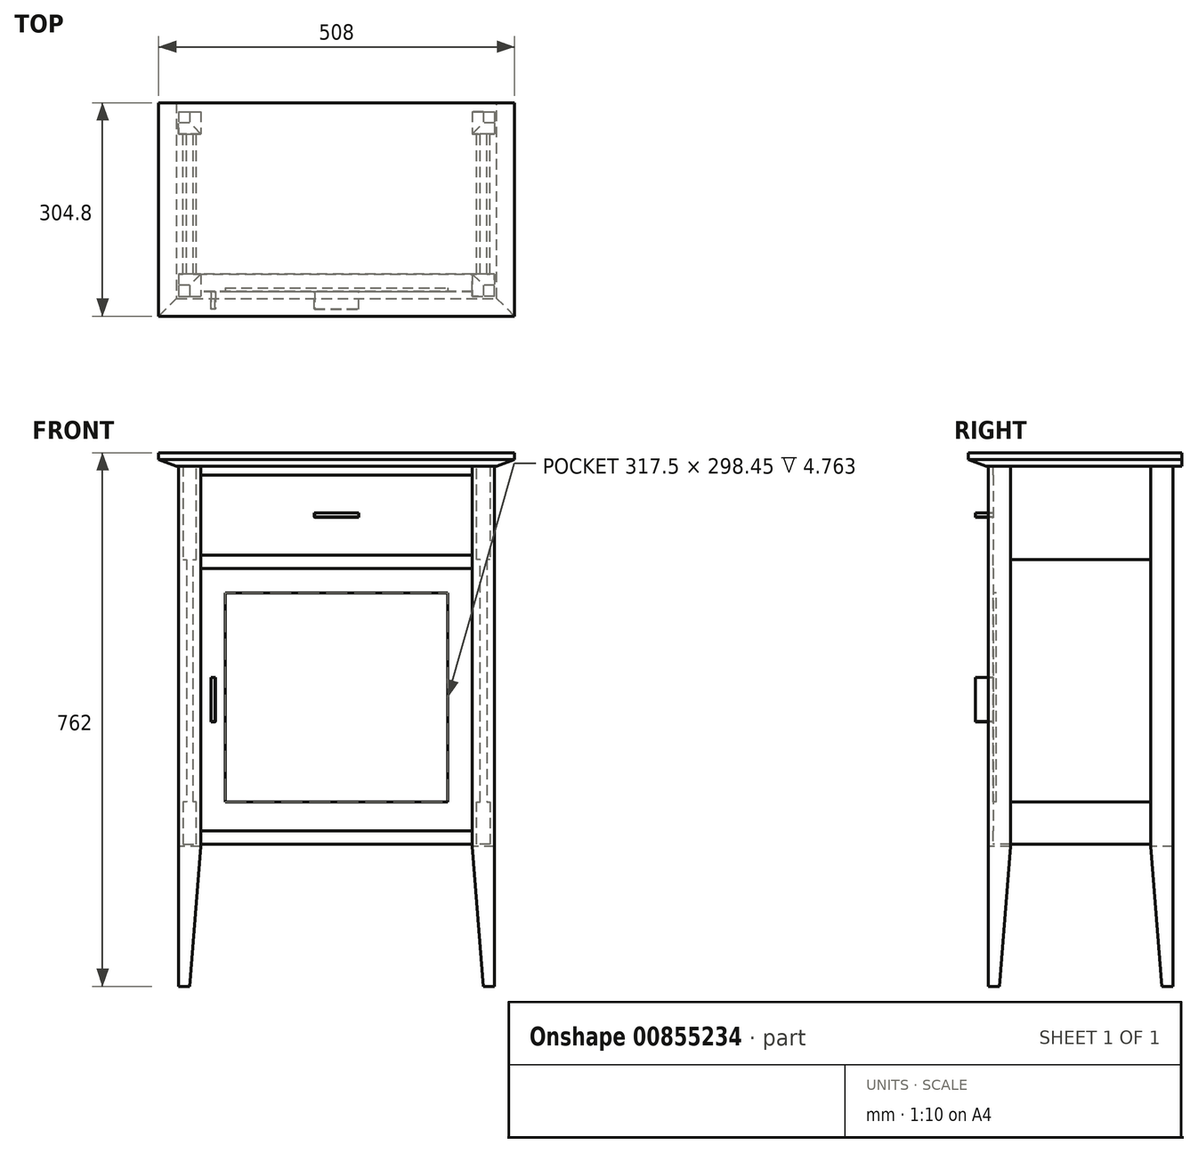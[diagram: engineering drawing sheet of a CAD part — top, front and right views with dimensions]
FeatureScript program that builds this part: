
annotation { "Feature Type Name" : "Feature", "Feature Type Description" : "" }
export const myFeature = defineFeature(function(context is Context, id is Id, definition is map)
    precondition{}
    {
        {
            var Q0;
            Q0=qCreatedBy(makeId("Top.planeOp"),FACE);
            var sketch = newSketch(context, id + "F0", { "sketchPlane" : qUnion([Q0])});
            skLineSegment(sketch, "E0", {"start": v(-209.55, 115.89) * mm, "end": v(209.55, 115.89) * mm, "construction": true});
            skLineSegment(sketch, "E1", {"start": v(209.55, 115.89) * mm, "end": v(209.55, -115.89) * mm, "construction": true});
            skLineSegment(sketch, "E2", {"start": v(209.55, -115.89) * mm, "end": v(-209.55, -115.89) * mm, "construction": true});
            skLineSegment(sketch, "E3", {"start": v(-209.55, -115.89) * mm, "end": v(-209.55, 115.89) * mm, "construction": true});
            skLineSegment(sketch, "E4", {"start": v(0, 115.89) * mm, "end": v(0, -115.89) * mm, "construction": true});
            skLineSegment(sketch, "E5", {"start": v(-209.55, 0) * mm, "end": v(209.55, 0) * mm, "construction": true});
            skPoint(sketch, "E6", {"position": v(0, 0) * mm});
            skLineSegment(sketch, "E7.bottom", {"start": v(-225.43, 131.76) * mm, "end": v(-193.68, 131.76) * mm});
            skLineSegment(sketch, "E7.top", {"start": v(-225.43, 100.01) * mm, "end": v(-193.68, 100.01) * mm});
            skLineSegment(sketch, "E7.left", {"start": v(-225.43, 131.76) * mm, "end": v(-225.43, 100.01) * mm});
            skLineSegment(sketch, "E7.right", {"start": v(-193.68, 131.76) * mm, "end": v(-193.68, 100.01) * mm});
            skPoint(sketch, "E7.middle", {"position": v(-209.55, 115.89) * mm});
            skLineSegment(sketch, "E8.bottom", {"start": v(193.67, 131.76) * mm, "end": v(225.42, 131.76) * mm});
            skLineSegment(sketch, "E8.top", {"start": v(193.67, 100.01) * mm, "end": v(225.42, 100.01) * mm});
            skLineSegment(sketch, "E8.left", {"start": v(193.67, 131.76) * mm, "end": v(193.67, 100.01) * mm});
            skLineSegment(sketch, "E8.right", {"start": v(225.42, 131.76) * mm, "end": v(225.42, 100.01) * mm});
            skPoint(sketch, "E8.middle", {"position": v(209.55, 115.89) * mm});
            skLineSegment(sketch, "E9.bottom", {"start": v(-225.42, -100.01) * mm, "end": v(-193.67, -100.01) * mm});
            skLineSegment(sketch, "E9.top", {"start": v(-225.42, -131.76) * mm, "end": v(-193.67, -131.76) * mm});
            skLineSegment(sketch, "E9.left", {"start": v(-225.42, -100.01) * mm, "end": v(-225.42, -131.76) * mm});
            skLineSegment(sketch, "E9.right", {"start": v(-193.67, -100.01) * mm, "end": v(-193.67, -131.76) * mm});
            skPoint(sketch, "E9.middle", {"position": v(-209.55, -115.89) * mm});
            skLineSegment(sketch, "E10.bottom", {"start": v(225.43, -131.76) * mm, "end": v(193.68, -131.76) * mm});
            skLineSegment(sketch, "E10.top", {"start": v(225.43, -100.01) * mm, "end": v(193.68, -100.01) * mm});
            skLineSegment(sketch, "E10.left", {"start": v(225.43, -131.76) * mm, "end": v(225.43, -100.01) * mm});
            skLineSegment(sketch, "E10.right", {"start": v(193.68, -131.76) * mm, "end": v(193.68, -100.01) * mm});
            skPoint(sketch, "E10.middle", {"position": v(209.55, -115.89) * mm});
            skSolve(sketch);
        }
        {
            var Q0;
            Q0 = qSketchRegion(id + "F0", true);
            extrude(context, id + "F1", {"entities" : qUnion([Q0]), "depth" : 742.95 * mm, "offsetDistance" : 25.4 * mm});
        }
        {
            var Q0;
            Q0=makeQuery(id+"F1.opExtrude","SWEPT_FACE",FACE,{"disambiguationData":[OSD([sQuery(id+"F0.wireOp",EDGE,"E7.top")])]});
            var sketch = newSketch(context, id + "F2", { "sketchPlane" : qUnion([Q0])});
            skLineSegment(sketch, "E11", {"start": v(-209.55, 742.95) * mm, "end": v(-209.55, 0) * mm, "construction": true});
            skLineSegment(sketch, "E12", {"start": v(-219.08, 742.95) * mm, "end": v(-219.08, 609.6) * mm});
            skLineSegment(sketch, "E13", {"start": v(-219.08, 609.6) * mm, "end": v(-200.03, 609.6) * mm});
            skLineSegment(sketch, "E14", {"start": v(-200.03, 609.6) * mm, "end": v(-200.03, 742.95) * mm});
            skLineSegment(sketch, "E15", {"start": v(-200.03, 742.95) * mm, "end": v(-219.08, 742.95) * mm});
            skLineSegment(sketch, "E16", {"start": v(-214.31, 609.6) * mm, "end": v(-214.31, 263.53) * mm});
            skLineSegment(sketch, "E17", {"start": v(-214.31, 263.53) * mm, "end": v(-204.79, 263.53) * mm});
            skLineSegment(sketch, "E18", {"start": v(-204.79, 263.53) * mm, "end": v(-204.79, 609.6) * mm});
            skLineSegment(sketch, "E19", {"start": v(-219.08, 263.53) * mm, "end": v(-219.08, 203.2) * mm});
            skLineSegment(sketch, "E20", {"start": v(-219.08, 203.2) * mm, "end": v(-200.03, 203.2) * mm});
            skLineSegment(sketch, "E21", {"start": v(-200.03, 203.2) * mm, "end": v(-200.03, 263.53) * mm});
            skLineSegment(sketch, "E22", {"start": v(-200.03, 263.53) * mm, "end": v(-219.08, 263.53) * mm});
            skLineSegment(sketch, "E23", {"start": v(-193.68, 0) * mm, "end": v(-193.68, 200.03) * mm});
            skLineSegment(sketch, "E24", {"start": v(-193.68, 200.03) * mm, "end": v(-209.55, 0) * mm});
            skLineSegment(sketch, "E25", {"start": v(-209.55, 0) * mm, "end": v(-193.68, 0) * mm});
            skLineSegment(sketch, "E26", {"start": v(0, 0) * mm, "end": v(0, 787.82) * mm, "construction": true});
            skLineSegment(sketch, "E27.MirrorCS", {"start": v(200.03, 742.95) * mm, "end": v(219.08, 742.95) * mm});
            skLineSegment(sketch, "E28.MirrorCS", {"start": v(219.08, 742.95) * mm, "end": v(219.08, 609.6) * mm});
            skLineSegment(sketch, "E29.MirrorCS", {"start": v(200.03, 609.6) * mm, "end": v(200.03, 742.95) * mm});
            skLineSegment(sketch, "E30.MirrorCS", {"start": v(219.08, 609.6) * mm, "end": v(200.03, 609.6) * mm});
            skLineSegment(sketch, "E31.MirrorCS", {"start": v(214.31, 609.6) * mm, "end": v(214.31, 263.53) * mm});
            skLineSegment(sketch, "E32.MirrorCS", {"start": v(204.79, 263.53) * mm, "end": v(204.79, 609.6) * mm});
            skLineSegment(sketch, "E33.MirrorCS", {"start": v(200.03, 263.53) * mm, "end": v(219.08, 263.53) * mm});
            skLineSegment(sketch, "E34.MirrorCS", {"start": v(219.08, 263.53) * mm, "end": v(219.08, 203.2) * mm});
            skLineSegment(sketch, "E35.MirrorCS", {"start": v(200.03, 203.2) * mm, "end": v(200.03, 263.53) * mm});
            skLineSegment(sketch, "E36.MirrorCS", {"start": v(219.08, 203.2) * mm, "end": v(200.03, 203.2) * mm});
            skLineSegment(sketch, "E37.MirrorCS", {"start": v(193.68, 200.03) * mm, "end": v(209.55, 0) * mm});
            skLineSegment(sketch, "E38.MirrorCS", {"start": v(193.68, 0) * mm, "end": v(193.68, 200.03) * mm});
            skLineSegment(sketch, "E39.MirrorCS", {"start": v(209.55, 0) * mm, "end": v(193.68, 0) * mm});
            skSolve(sketch);
        }
        {
            var Q0;
            {var subQ3=sQuery(id+"F2.wireOp",EDGE,"E19");Q0=makeQuery(id+"F2.imprint","IMPRINT",FACE,{"disambiguationData":[TD([[makeQuery(id+"F2.imprint","IMPRINT",EDGE,{"derivedFrom":subQ3}),1.0]])]});}
            var Q1;
            {var subQ0=sQuery(id+"F2.wireOp",EDGE,"E16");Q1=makeQuery(id+"F2.imprint","IMPRINT",FACE,{"disambiguationData":[TD([[makeQuery(id+"F2.imprint","IMPRINT",EDGE,{"derivedFrom":subQ0}),1.0]])]});}
            var Q2;
            {var subQ4=sQuery(id+"F2.wireOp",EDGE,"E12");Q2=makeQuery(id+"F2.imprint","IMPRINT",FACE,{"disambiguationData":[TD([[makeQuery(id+"F2.imprint","IMPRINT",EDGE,{"derivedFrom":subQ4}),1.0]])]});}
            var Q3;
            Q3=makeQuery(id+"F2.imprint","IMPRINT",FACE,{"disambiguationData":[TD([[makeQuery(id+"F2.imprint","IMPRINT",EDGE,{"derivedFrom":sQuery(id+"F2.wireOp",EDGE,"E27.MirrorCS")}),-1.0]])]});
            var Q4;
            {var subQ0=sQuery(id+"F2.wireOp",EDGE,"E31.MirrorCS");Q4=makeQuery(id+"F2.imprint","IMPRINT",FACE,{"disambiguationData":[TD([[makeQuery(id+"F2.imprint","IMPRINT",EDGE,{"derivedFrom":subQ0}),-1.0]])]});}
            var Q5;
            {var subQ0=sQuery(id+"F2.wireOp",EDGE,"E34.MirrorCS");Q5=makeQuery(id+"F2.imprint","IMPRINT",FACE,{"disambiguationData":[TD([[makeQuery(id+"F2.imprint","IMPRINT",EDGE,{"derivedFrom":subQ0}),-1.0]])]});}
            extrude(context, id + "F3", {"entities" : qUnion([Q0, Q1, Q2, Q3, Q4, Q5]), "operationType" : NewBodyOperationType.ADD, "endBound" : BoundingType.UP_TO_NEXT, "depth" : 25.4 * mm, "offsetDistance" : 25.4 * mm});
        }
        {
            var Q0;
            Q0=makeQuery(id+"F2.imprint","IMPRINT",FACE,{"disambiguationData":[TD([[makeQuery(id+"F2.imprint","IMPRINT",EDGE,{"derivedFrom":sQuery(id+"F2.wireOp",EDGE,"E23")}),-1.0]])]});
            var Q1;
            Q1=makeQuery(id+"F2.imprint","IMPRINT",FACE,{"disambiguationData":[TD([[makeQuery(id+"F2.imprint","IMPRINT",EDGE,{"derivedFrom":sQuery(id+"F2.wireOp",EDGE,"E37.MirrorCS")}),-1.0]])]});
            extrude(context, id + "F4", {"entities" : qUnion([Q0, Q1]), "operationType" : NewBodyOperationType.REMOVE, "endBound" : BoundingType.THROUGH_ALL, "oppositeDirection" : true, "depth" : 25.4 * mm, "offsetDistance" : 25.4 * mm, "hasSecondDirection" : true, "secondDirectionBound" : SecondDirectionBoundingType.THROUGH_ALL, "secondDirectionOppositeDirection" : false, "secondDirectionDepth" : 25.4 * mm});
        }
        {
            var Q0;
            Q0=makeQuery(id+"F1.opExtrude","SWEPT_FACE",FACE,{"disambiguationData":[OSD([sQuery(id+"F0.wireOp",EDGE,"E9.left")])]});
            var sketch = newSketch(context, id + "F5", { "sketchPlane" : qUnion([Q0])});
            skLineSegment(sketch, "E40", {"start": v(100.01, 200.03) * mm, "end": v(115.89, 0) * mm});
            skLineSegment(sketch, "E41", {"start": v(115.89, 0) * mm, "end": v(100.01, 0) * mm});
            skLineSegment(sketch, "E42", {"start": v(100.01, 0) * mm, "end": v(100.01, 200.03) * mm});
            skLineSegment(sketch, "E43", {"start": v(0, 0) * mm, "end": v(0, 281.06) * mm, "construction": true});
            skLineSegment(sketch, "E44.MirrorCS", {"start": v(-100.01, 200.03) * mm, "end": v(-115.89, 0) * mm});
            skLineSegment(sketch, "E45.MirrorCS", {"start": v(-100.01, 0) * mm, "end": v(-100.01, 200.03) * mm});
            skLineSegment(sketch, "E46.MirrorCS", {"start": v(-115.89, 0) * mm, "end": v(-100.01, 0) * mm});
            skSolve(sketch);
        }
        {
            var Q0;
            Q0 = qSketchRegion(id + "F5", true);
            extrude(context, id + "F6", {"entities" : qUnion([Q0]), "operationType" : NewBodyOperationType.REMOVE, "endBound" : BoundingType.THROUGH_ALL, "oppositeDirection" : true, "depth" : 25.4 * mm, "offsetDistance" : 25.4 * mm});
        }
        {
            var Q0;
            Q0=makeQuery(id+"F1.opExtrude","SWEPT_FACE",FACE,{"disambiguationData":[OSD([sQuery(id+"F0.wireOp",EDGE,"E9.right")])]});
            var sketch = newSketch(context, id + "F7", { "sketchPlane" : qUnion([Q0])});
            skLineSegment(sketch, "E47.bottom", {"start": v(-100.01, 742.95) * mm, "end": v(-125.41, 742.95) * mm});
            skLineSegment(sketch, "E47.top", {"start": v(-100.01, 730.25) * mm, "end": v(-125.41, 730.25) * mm});
            skLineSegment(sketch, "E47.left", {"start": v(-100.01, 742.95) * mm, "end": v(-100.01, 730.25) * mm});
            skLineSegment(sketch, "E47.right", {"start": v(-125.41, 742.95) * mm, "end": v(-125.41, 730.25) * mm});
            skLineSegment(sketch, "E48.bottom", {"start": v(-100.01, 615.95) * mm, "end": v(-125.41, 615.95) * mm});
            skLineSegment(sketch, "E48.top", {"start": v(-100.01, 596.9) * mm, "end": v(-125.41, 596.9) * mm});
            skLineSegment(sketch, "E48.left", {"start": v(-100.01, 615.95) * mm, "end": v(-100.01, 596.9) * mm});
            skLineSegment(sketch, "E48.right", {"start": v(-125.41, 615.95) * mm, "end": v(-125.41, 596.9) * mm});
            skLineSegment(sketch, "E49", {"start": v(-125.02, 730.25) * mm, "end": v(-125.02, 615.95) * mm});
            skLineSegment(sketch, "E50", {"start": v(-100.01, 615.95) * mm, "end": v(-100.01, 730.25) * mm});
            skLineSegment(sketch, "E51.bottom", {"start": v(-100.01, 222.25) * mm, "end": v(-125.41, 222.25) * mm});
            skLineSegment(sketch, "E51.top", {"start": v(-100.01, 203.2) * mm, "end": v(-125.41, 203.2) * mm});
            skLineSegment(sketch, "E51.left", {"start": v(-100.01, 222.25) * mm, "end": v(-100.01, 203.2) * mm});
            skLineSegment(sketch, "E51.right", {"start": v(-125.41, 222.25) * mm, "end": v(-125.41, 203.2) * mm});
            skLineSegment(sketch, "E52", {"start": v(-125.02, 596.9) * mm, "end": v(-125.02, 222.25) * mm});
            skLineSegment(sketch, "E53", {"start": v(-100.01, 222.25) * mm, "end": v(-100.01, 596.9) * mm});
            skSolve(sketch);
        }
        {
            var Q0;
            Q0 = qSketchRegion(id + "F7", true);
            extrude(context, id + "F8", {"entities" : qUnion([Q0]), "operationType" : NewBodyOperationType.ADD, "endBound" : BoundingType.UP_TO_NEXT, "depth" : 25.4 * mm, "offsetDistance" : 25.4 * mm});
        }
        {
            var Q0;
            Q0=makeQuery(id+"F8.opExtrude","SWEPT_FACE",FACE,{"disambiguationData":[OSD([sQuery(id+"F7.wireOp",EDGE,"E52")])]});
            var sketch = newSketch(context, id + "F9", { "sketchPlane" : qUnion([Q0])});
            skLineSegment(sketch, "E54.0", {"start": v(-158.75, 257.18) * mm, "end": v(158.75, 257.18) * mm});
            skLineSegment(sketch, "E54.1", {"start": v(-158.75, 561.98) * mm, "end": v(-158.75, 257.18) * mm});
            skLineSegment(sketch, "E54.2", {"start": v(158.75, 561.98) * mm, "end": v(-158.75, 561.98) * mm});
            skLineSegment(sketch, "E54.3", {"start": v(158.75, 257.18) * mm, "end": v(158.75, 561.98) * mm});
            skLineSegment(sketch, "E55", {"start": v(-158.75, 263.53) * mm, "end": v(158.75, 263.53) * mm});
            skSolve(sketch);
        }
        {
            var Q0;
            {var subQ0=sQuery(id+"F9.wireOp",EDGE,"E54.2");Q0=makeQuery(id+"F9.imprint","IMPRINT",FACE,{"disambiguationData":[TD([[makeQuery(id+"F9.imprint","IMPRINT",EDGE,{"derivedFrom":subQ0}),1.0]])]});}
            extrude(context, id + "F10", {"entities" : qUnion([Q0]), "operationType" : NewBodyOperationType.REMOVE, "oppositeDirection" : true, "depth" : 4.76 * mm, "offsetDistance" : 25.4 * mm});
        }
        {
            var Q0;
            Q0=makeQuery(id+"F8.boolean.opBoolean","MERGE",FACE,{"derivedFrom":[makeQuery(id+"F3.boolean.opBoolean","MERGE",FACE,{"derivedFrom":[makeQuery(id+"F1.opExtrude","CAP_FACE",FACE,{"disambiguationData":[OSD([sQuery(id+"F0.wireOp",EDGE,"E7.bottom"),sQuery(id+"F0.wireOp",EDGE,"E7.top"),sQuery(id+"F0.wireOp",EDGE,"E7.left"),sQuery(id+"F0.wireOp",EDGE,"E7.right")])],"isStart":false}),makeQuery(id+"F1.opExtrude","CAP_FACE",FACE,{"disambiguationData":[OSD([sQuery(id+"F0.wireOp",EDGE,"E9.bottom"),sQuery(id+"F0.wireOp",EDGE,"E9.top"),sQuery(id+"F0.wireOp",EDGE,"E9.left"),sQuery(id+"F0.wireOp",EDGE,"E9.right")])],"isStart":false}),makeQuery(id+"F3.opExtrude","SWEPT_FACE",FACE,{"disambiguationData":[OSD([sQuery(id+"F2.wireOp",EDGE,"E15")])]})]}),makeQuery(id+"F3.boolean.opBoolean","MERGE",FACE,{"derivedFrom":[makeQuery(id+"F1.opExtrude","CAP_FACE",FACE,{"disambiguationData":[OSD([sQuery(id+"F0.wireOp",EDGE,"E8.bottom"),sQuery(id+"F0.wireOp",EDGE,"E8.top"),sQuery(id+"F0.wireOp",EDGE,"E8.left"),sQuery(id+"F0.wireOp",EDGE,"E8.right")])],"isStart":false}),makeQuery(id+"F1.opExtrude","CAP_FACE",FACE,{"disambiguationData":[OSD([sQuery(id+"F0.wireOp",EDGE,"E10.bottom"),sQuery(id+"F0.wireOp",EDGE,"E10.top"),sQuery(id+"F0.wireOp",EDGE,"E10.left"),sQuery(id+"F0.wireOp",EDGE,"E10.right")])],"isStart":false}),makeQuery(id+"F3.opExtrude","SWEPT_FACE",FACE,{"disambiguationData":[OSD([sQuery(id+"F2.wireOp",EDGE,"E27.MirrorCS")])]})]}),makeQuery(id+"F8.opExtrude","SWEPT_FACE",FACE,{"disambiguationData":[OSD([sQuery(id+"F7.wireOp",EDGE,"E47.bottom")])]})]});
            var sketch = newSketch(context, id + "F11", { "sketchPlane" : qUnion([Q0])});
            skLineSegment(sketch, "E56", {"start": v(0, 137.26) * mm, "end": v(0, -185.37) * mm, "construction": true});
            skLineSegment(sketch, "E57", {"start": v(-177.63, 0) * mm, "end": v(186.24, 0) * mm, "construction": true});
            skLineSegment(sketch, "E58", {"start": v(-254, 144.46) * mm, "end": v(254, 144.46) * mm});
            skLineSegment(sketch, "E59", {"start": v(254, 144.46) * mm, "end": v(254, -160.34) * mm});
            skLineSegment(sketch, "E60", {"start": v(254, -160.34) * mm, "end": v(-254, -160.34) * mm});
            skLineSegment(sketch, "E61", {"start": v(-254, -160.34) * mm, "end": v(-254, 144.46) * mm});
            skSolve(sketch);
        }
        {
            var Q0;
            Q0 = qSketchRegion(id + "F11", true);
            extrude(context, id + "F12", {"entities" : qUnion([Q0]), "operationType" : NewBodyOperationType.ADD, "depth" : 19.05 * mm, "offsetDistance" : 25.4 * mm});
        }
        {
            var Q0;
            Q0=makeQuery(id+"F12.opExtrude","SWEPT_FACE",FACE,{"disambiguationData":[OSD([sQuery(id+"F11.wireOp",EDGE,"E58")])]});
            var sketch = newSketch(context, id + "F13", { "sketchPlane" : qUnion([Q0])});
            skLineSegment(sketch, "E62", {"start": v(228.6, 742.95) * mm, "end": v(254, 752.48) * mm});
            skLineSegment(sketch, "E63", {"start": v(254, 752.48) * mm, "end": v(254, 742.95) * mm});
            skLineSegment(sketch, "E64", {"start": v(254, 742.95) * mm, "end": v(228.6, 742.95) * mm});
            skSolve(sketch);
        }
        {
            var Q0;
            Q0=makeQuery(id+"F13.imprint","IMPRINT",FACE,{"disambiguationData":[TD([[makeQuery(id+"F13.imprint","IMPRINT",EDGE,{"derivedFrom":sQuery(id+"F13.wireOp",EDGE,"E62")}),-1.0]])]});
            var Q1;
            Q1=makeQuery(id+"F1NDxMYOyf2uWx9_1.boolean.opBoolean","MERGE",EDGE,{"derivedFrom":[makeQuery(id+"F12.opExtrude","CAP_EDGE",EDGE,{"disambiguationData":[OSD([sQuery(id+"F11.wireOp",EDGE,"E61")])],"isStart":true}),makeQuery(id+"F1NDxMYOyf2uWx9_1.opExtrude","SWEPT_EDGE",EDGE,{"disambiguationData":[OSD([sQuery(id+"F13.wireOp",EDGE,"E63"),sQuery(id+"F13.wireOp",EDGE,"E64")])]})]});
            var Q2;
            Q2=makeQuery(id+"F12.opExtrude","CAP_EDGE",EDGE,{"disambiguationData":[OSD([sQuery(id+"F11.wireOp",EDGE,"E60")])],"isStart":true});
            var Q3;
            Q3=makeQuery(id+"F12.opExtrude","CAP_EDGE",EDGE,{"disambiguationData":[OSD([sQuery(id+"F11.wireOp",EDGE,"E59")])],"isStart":true});
            sweep(context, id + "F14", {"operationType" : NewBodyOperationType.REMOVE, "profiles" : qUnion([Q0]), "path" : qUnion([Q1, Q2, Q3])});
        }
        {
            var Q0;
            Q0=makeQuery(id+"F8.opExtrude","SWEPT_FACE",FACE,{"disambiguationData":[OSD([sQuery(id+"F7.wireOp",EDGE,"E49")])]});
            var sketch = newSketch(context, id + "F15", { "sketchPlane" : qUnion([Q0])});
            skLineSegment(sketch, "E65", {"start": v(0, 730.25) * mm, "end": v(0, 110.09) * mm, "construction": true});
            skLineSegment(sketch, "E66", {"start": v(-193.67, 673.1) * mm, "end": v(193.67, 673.1) * mm, "construction": true});
            skLineSegment(sketch, "E67", {"start": v(-176.21, 596.9) * mm, "end": v(-176.21, 222.25) * mm, "construction": true});
            skLineSegment(sketch, "E68.bottom", {"start": v(-31.75, 676.27) * mm, "end": v(31.75, 676.27) * mm});
            skLineSegment(sketch, "E68.top", {"start": v(-31.75, 669.92) * mm, "end": v(31.75, 669.92) * mm});
            skLineSegment(sketch, "E68.left", {"start": v(-31.75, 676.27) * mm, "end": v(-31.75, 669.92) * mm});
            skLineSegment(sketch, "E68.right", {"start": v(31.75, 676.27) * mm, "end": v(31.75, 669.92) * mm});
            skPoint(sketch, "E68.middle", {"position": v(0, 673.1) * mm});
            skLineSegment(sketch, "E69.bottom", {"start": v(-173.04, 441.32) * mm, "end": v(-179.39, 441.32) * mm});
            skLineSegment(sketch, "E69.top", {"start": v(-173.04, 377.82) * mm, "end": v(-179.39, 377.82) * mm});
            skLineSegment(sketch, "E69.left", {"start": v(-173.04, 441.32) * mm, "end": v(-173.04, 377.82) * mm});
            skLineSegment(sketch, "E69.right", {"start": v(-179.39, 441.32) * mm, "end": v(-179.39, 377.82) * mm});
            skPoint(sketch, "E69.middle", {"position": v(-176.21, 409.58) * mm});
            skSolve(sketch);
        }
        {
            var Q0;
            Q0 = qSketchRegion(id + "F15", true);
            extrude(context, id + "F16", {"entities" : qUnion([Q0]), "operationType" : NewBodyOperationType.ADD, "depth" : 25.4 * mm, "offsetDistance" : 25.4 * mm});
        }
        {
            var Q0;
            Q0=makeQuery(id+"F16.opExtrude","SWEPT_EDGE",EDGE,{"disambiguationData":[OSD([sQuery(id+"F15.wireOp",EDGE,"E68.bottom"),sQuery(id+"F15.wireOp",EDGE,"E68.left")])]});
            var Q1;
            Q1=makeQuery(id+"F16.opExtrude","CAP_EDGE",EDGE,{"disambiguationData":[OSD([sQuery(id+"F15.wireOp",EDGE,"E68.bottom")])],"isStart":false});
            var Q2;
            Q2=makeQuery(id+"F16.opExtrude","SWEPT_EDGE",EDGE,{"disambiguationData":[OSD([sQuery(id+"F15.wireOp",EDGE,"E68.bottom"),sQuery(id+"F15.wireOp",EDGE,"E68.right")])]});
            var Q3;
            Q3=makeQuery(id+"F16.opExtrude","SWEPT_EDGE",EDGE,{"disambiguationData":[OSD([sQuery(id+"F15.wireOp",EDGE,"E68.top"),sQuery(id+"F15.wireOp",EDGE,"E68.left")])]});
            var Q4;
            Q4=makeQuery(id+"F16.opExtrude","CAP_EDGE",EDGE,{"disambiguationData":[OSD([sQuery(id+"F15.wireOp",EDGE,"E68.top")])],"isStart":false});
            var Q5;
            Q5=makeQuery(id+"F16.opExtrude","SWEPT_EDGE",EDGE,{"disambiguationData":[OSD([sQuery(id+"F15.wireOp",EDGE,"E68.top"),sQuery(id+"F15.wireOp",EDGE,"E68.right")])]});
            var Q6;
            Q6=makeQuery(id+"F16.opExtrude","CAP_EDGE",EDGE,{"disambiguationData":[OSD([sQuery(id+"F15.wireOp",EDGE,"E68.left")])],"isStart":false});
            var Q7;
            Q7=makeQuery(id+"F16.opExtrude","CAP_EDGE",EDGE,{"disambiguationData":[OSD([sQuery(id+"F15.wireOp",EDGE,"E68.right")])],"isStart":false});
            var Q8;
            Q8=makeQuery(id+"F16.opExtrude","SWEPT_EDGE",EDGE,{"disambiguationData":[OSD([sQuery(id+"F15.wireOp",EDGE,"E69.bottom"),sQuery(id+"F15.wireOp",EDGE,"E69.right")])]});
            var Q9;
            Q9=makeQuery(id+"F16.opExtrude","SWEPT_EDGE",EDGE,{"disambiguationData":[OSD([sQuery(id+"F15.wireOp",EDGE,"E69.bottom"),sQuery(id+"F15.wireOp",EDGE,"E69.left")])]});
            var Q10;
            Q10=makeQuery(id+"F16.opExtrude","CAP_EDGE",EDGE,{"disambiguationData":[OSD([sQuery(id+"F15.wireOp",EDGE,"E69.right")])],"isStart":false});
            var Q11;
            Q11=makeQuery(id+"F16.opExtrude","CAP_EDGE",EDGE,{"disambiguationData":[OSD([sQuery(id+"F15.wireOp",EDGE,"E69.left")])],"isStart":false});
            var Q12;
            Q12=makeQuery(id+"F16.opExtrude","CAP_EDGE",EDGE,{"disambiguationData":[OSD([sQuery(id+"F15.wireOp",EDGE,"E69.bottom")])],"isStart":false});
            var Q13;
            Q13=makeQuery(id+"F16.opExtrude","CAP_EDGE",EDGE,{"disambiguationData":[OSD([sQuery(id+"F15.wireOp",EDGE,"E69.top")])],"isStart":false});
            var Q14;
            Q14=makeQuery(id+"F16.opExtrude","SWEPT_EDGE",EDGE,{"disambiguationData":[OSD([sQuery(id+"F15.wireOp",EDGE,"E69.top"),sQuery(id+"F15.wireOp",EDGE,"E69.right")])]});
            var Q15;
            Q15=makeQuery(id+"F16.opExtrude","SWEPT_EDGE",EDGE,{"disambiguationData":[OSD([sQuery(id+"F15.wireOp",EDGE,"E69.top"),sQuery(id+"F15.wireOp",EDGE,"E69.left")])]});
            chamfer(context, id + "F17", {"entities" : qUnion([Q0, Q1, Q2, Q3, Q4, Q5, Q6, Q7, Q8, Q9, Q10, Q11, Q12, Q13, Q14, Q15]), "width" : 0.32 * mm, "tangentPropagation" : true});
        }
    });
